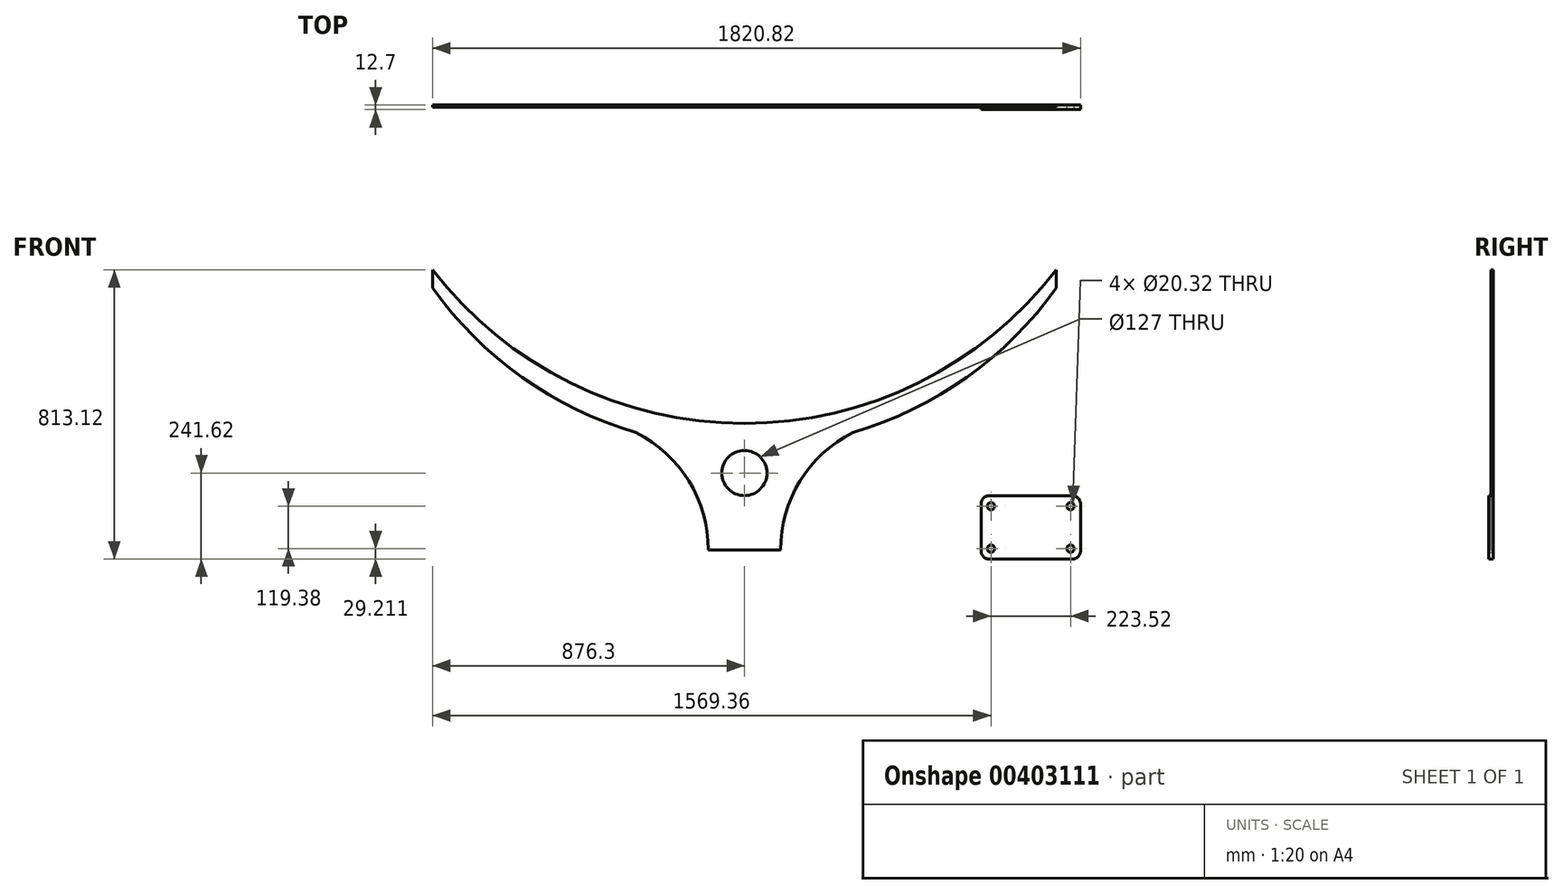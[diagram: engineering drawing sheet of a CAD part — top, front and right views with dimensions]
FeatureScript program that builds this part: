
annotation { "Feature Type Name" : "Feature", "Feature Type Description" : "" }
export const myFeature = defineFeature(function(context is Context, id is Id, definition is map)
    precondition{}
    {
        {
            var Q0;
            Q0=qCreatedBy(makeId("Front.planeOp"),FACE);
            var sketch = newSketch(context, id + "F0", { "sketchPlane" : qUnion([Q0])});
            skLineSegment(sketch, "E0", {"start": v(0, 0) * mm, "end": v(-876.3, 0) * mm});
            skLineSegment(sketch, "E1", {"start": v(0, 0) * mm, "end": v(876.3, 0) * mm});
            skLineSegment(sketch, "E2", {"start": v(0, 0) * mm, "end": v(0, -431.8) * mm});
            skArc(sketch, "E3", {"start": v(-876.3, 0) * mm, "mid": v(0, -431.8) * mm, "end": v(876.3, 0) * mm});
            skLineSegment(sketch, "E4", {"start": v(-876.3, 0) * mm, "end": v(-876.3, -50.8) * mm});
            skLineSegment(sketch, "E5", {"start": v(876.3, 0) * mm, "end": v(876.3, -50.8) * mm});
            skLineSegment(sketch, "E6.bottom", {"start": v(0, -431.8) * mm, "end": v(-101.6, -431.8) * mm});
            skLineSegment(sketch, "E6.top", {"start": v(0, -787.4) * mm, "end": v(-101.6, -787.4) * mm});
            skLineSegment(sketch, "E6.left", {"start": v(0, -431.8) * mm, "end": v(0, -787.4) * mm});
            skLineSegment(sketch, "E6.right", {"start": v(-101.6, -431.8) * mm, "end": v(-101.6, -787.4) * mm});
            skLineSegment(sketch, "E7.bottom", {"start": v(0, -431.8) * mm, "end": v(101.6, -431.8) * mm});
            skLineSegment(sketch, "E7.top", {"start": v(0, -787.4) * mm, "end": v(101.6, -787.4) * mm});
            skLineSegment(sketch, "E7.right", {"start": v(101.6, -431.8) * mm, "end": v(101.6, -787.4) * mm});
            skLineSegment(sketch, "E8", {"start": v(304.8, -457.2) * mm, "end": v(-304.8, -457.2) * mm});
            skArc(sketch, "E9", {"start": v(-876.3, -50.8) * mm, "mid": v(-624.9, -302.3) * mm, "end": v(-304.8, -457.2) * mm});
            skArc(sketch, "E10", {"start": v(304.8, -457.2) * mm, "mid": v(624.9, -302.3) * mm, "end": v(876.3, -50.8) * mm});
            skArc(sketch, "E11", {"start": v(-101.6, -787.4) * mm, "mid": v(-156.47, -593.54) * mm, "end": v(-304.8, -457.2) * mm});
            skArc(sketch, "E12", {"start": v(304.8, -457.2) * mm, "mid": v(156.47, -593.54) * mm, "end": v(101.6, -787.4) * mm});
            skCircle(sketch, "E13", {"center": v(0, -571.5) * mm, "radius": 63.5 * mm});
            skSolve(sketch);
        }
        {
            var Q0;
            {var subQ5=sQuery(id+"F0.wireOp",EDGE,"E4");Q0=makeQuery(id+"F0.imprint","IMPRINT",FACE,{"disambiguationData":[TD([[makeQuery(id+"F0.imprint","IMPRINT",EDGE,{"derivedFrom":subQ5}),1.0]])]});}
            var Q1;
            {var subQ0=sQuery(id+"F0.wireOp",EDGE,"E11");Q1=makeQuery(id+"F0.imprint","IMPRINT",FACE,{"disambiguationData":[TD([[makeQuery(id+"F0.imprint","IMPRINT",EDGE,{"derivedFrom":subQ0}),-1.0]])]});}
            var Q2;
            {var subQ0=sQuery(id+"F0.wireOp",EDGE,"E6.top");Q2=makeQuery(id+"F0.imprint","IMPRINT",FACE,{"disambiguationData":[TD([[makeQuery(id+"F0.imprint","IMPRINT",EDGE,{"derivedFrom":subQ0}),-1.0]])]});}
            var Q3;
            {var subQ0=sQuery(id+"F0.wireOp",EDGE,"E7.top");Q3=makeQuery(id+"F0.imprint","IMPRINT",FACE,{"disambiguationData":[TD([[makeQuery(id+"F0.imprint","IMPRINT",EDGE,{"derivedFrom":subQ0}),1.0]])]});}
            var Q4;
            {var subQ0=sQuery(id+"F0.wireOp",EDGE,"E6.bottom");Q4=makeQuery(id+"F0.imprint","IMPRINT",FACE,{"disambiguationData":[TD([[makeQuery(id+"F0.imprint","IMPRINT",EDGE,{"derivedFrom":subQ0}),1.0]])]});}
            var Q5;
            {var subQ0=sQuery(id+"F0.wireOp",EDGE,"E7.bottom");Q5=makeQuery(id+"F0.imprint","IMPRINT",FACE,{"disambiguationData":[TD([[makeQuery(id+"F0.imprint","IMPRINT",EDGE,{"derivedFrom":subQ0}),-1.0]])]});}
            var Q6;
            {var subQ4=sQuery(id+"F0.wireOp",EDGE,"E5");Q6=makeQuery(id+"F0.imprint","IMPRINT",FACE,{"disambiguationData":[TD([[makeQuery(id+"F0.imprint","IMPRINT",EDGE,{"derivedFrom":subQ4}),-1.0]])]});}
            var Q7;
            {var subQ0=sQuery(id+"F0.wireOp",EDGE,"E12");Q7=makeQuery(id+"F0.imprint","IMPRINT",FACE,{"disambiguationData":[TD([[makeQuery(id+"F0.imprint","IMPRINT",EDGE,{"derivedFrom":subQ0}),-1.0]])]});}
            extrude(context, id + "F1", {"entities" : qUnion([Q0, Q1, Q2, Q3, Q4, Q5, Q6, Q7]), "depth" : 6.35 * mm});
        }
        {
            var Q0;
            Q0=qCreatedBy(makeId("Front.planeOp"),FACE);
            var sketch = newSketch(context, id + "F2", { "sketchPlane" : qUnion([Q0])});
            skLineSegment(sketch, "E14.bottom", {"start": v(665.12, -635.32) * mm, "end": v(944.52, -635.32) * mm});
            skLineSegment(sketch, "E14.top", {"start": v(665.12, -813.12) * mm, "end": v(944.52, -813.12) * mm});
            skLineSegment(sketch, "E14.left", {"start": v(665.12, -635.32) * mm, "end": v(665.12, -813.12) * mm});
            skLineSegment(sketch, "E14.right", {"start": v(944.52, -635.32) * mm, "end": v(944.52, -813.12) * mm});
            skCircle(sketch, "E15", {"center": v(693.06, -664.53) * mm, "radius": 10.16 * mm});
            skCircle(sketch, "E16", {"center": v(916.58, -664.53) * mm, "radius": 10.16 * mm});
            skCircle(sketch, "E17", {"center": v(693.06, -783.9) * mm, "radius": 10.16 * mm});
            skCircle(sketch, "E18", {"center": v(916.58, -783.9) * mm, "radius": 10.16 * mm});
            skSolve(sketch);
        }
        {
            var Q0;
            Q0=makeQuery(id+"F2.imprint","IMPRINT",FACE,{"disambiguationData":[TD([[makeQuery(id+"F2.imprint","IMPRINT",EDGE,{"derivedFrom":sQuery(id+"F2.wireOp",EDGE,"E14.bottom")}),-1.0]])]});
            extrude(context, id + "F3", {"entities" : qUnion([Q0]), "depth" : 12.7 * mm});
        }
        {
            var Q0;
            Q0=makeQuery(id+"F3.opExtrude","SWEPT_EDGE",EDGE,{"disambiguationData":[OSD([sQuery(id+"F2.wireOp",EDGE,"E14.bottom"),sQuery(id+"F2.wireOp",EDGE,"E14.left")])]});
            var Q1;
            Q1=makeQuery(id+"F3.opExtrude","SWEPT_EDGE",EDGE,{"disambiguationData":[OSD([sQuery(id+"F2.wireOp",EDGE,"E14.top"),sQuery(id+"F2.wireOp",EDGE,"E14.left")])]});
            var Q2;
            Q2=makeQuery(id+"F3.opExtrude","SWEPT_EDGE",EDGE,{"disambiguationData":[OSD([sQuery(id+"F2.wireOp",EDGE,"E14.bottom"),sQuery(id+"F2.wireOp",EDGE,"E14.right")])]});
            var Q3;
            Q3=makeQuery(id+"F3.opExtrude","SWEPT_EDGE",EDGE,{"disambiguationData":[OSD([sQuery(id+"F2.wireOp",EDGE,"E14.top"),sQuery(id+"F2.wireOp",EDGE,"E14.right")])]});
            fillet(context, id + "F4", {"entities" : qUnion([Q0, Q1, Q2, Q3]), "radius" : 22.7 * mm, "tangentPropagation" : true, "allowEdgeOverflow" : false});
        }
    });
